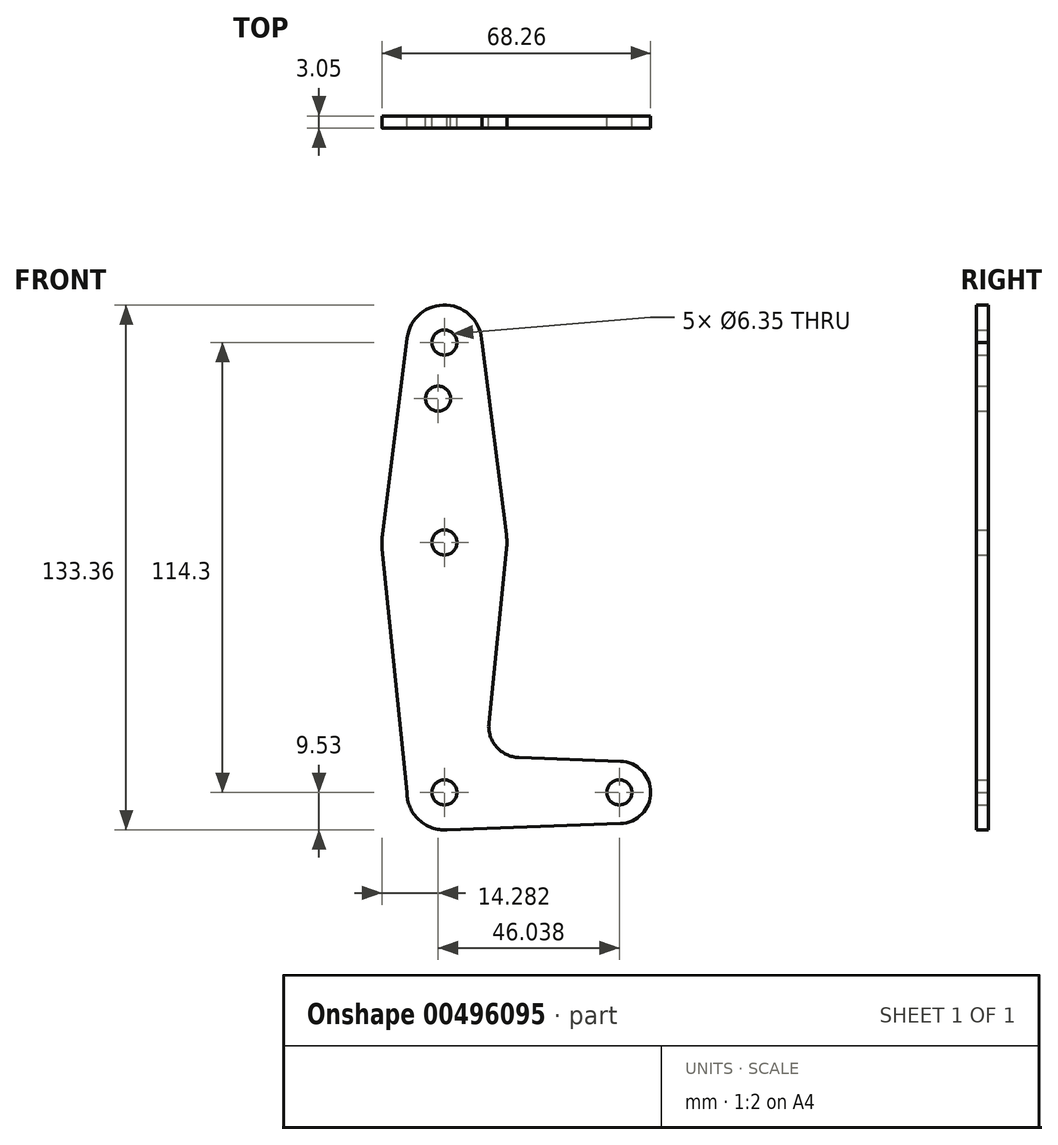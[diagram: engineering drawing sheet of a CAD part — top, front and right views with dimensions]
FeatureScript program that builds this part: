
annotation { "Feature Type Name" : "Feature", "Feature Type Description" : "" }
export const myFeature = defineFeature(function(context is Context, id is Id, definition is map)
    precondition{}
    {
        {
            var Q0;
            Q0=qCreatedBy(makeId("Front.planeOp"),FACE);
            var sketch = newSketch(context, id + "F0", { "sketchPlane" : qUnion([Q0])});
            skLineSegment(sketch, "E0", {"start": v(0, 114.3) * mm, "end": v(0, 0) * mm, "construction": true});
            skLineSegment(sketch, "E1", {"start": v(0, 0) * mm, "end": v(44.45, 0) * mm, "construction": true});
            skCircle(sketch, "E2", {"center": v(0, 0) * mm, "radius": 9.53 * mm});
            skCircle(sketch, "E3", {"center": v(44.45, 0) * mm, "radius": 7.94 * mm});
            skCircle(sketch, "E4", {"center": v(0, 63.5) * mm, "radius": 15.88 * mm});
            skCircle(sketch, "E5", {"center": v(0, 114.3) * mm, "radius": 9.53 * mm});
            skLineSegment(sketch, "E6", {"start": v(9.52, 114.3) * mm, "end": v(15.75, 65.5) * mm});
            skLineSegment(sketch, "E7", {"start": v(-9.45, 115.5) * mm, "end": v(-15.75, 65.48) * mm});
            skLineSegment(sketch, "E8", {"start": v(15.8, 61.9) * mm, "end": v(11.3, 17.6) * mm});
            skLineSegment(sketch, "E9", {"start": v(-15.8, 61.9) * mm, "end": v(-9.52, 0) * mm});
            skLineSegment(sketch, "E10", {"start": v(44.73, 7.93) * mm, "end": v(18.93, 8.85) * mm});
            skCircle(sketch, "E11", {"center": v(0, 114.3) * mm, "radius": 3.18 * mm});
            skCircle(sketch, "E12", {"center": v(0, 63.5) * mm, "radius": 3.18 * mm});
            skCircle(sketch, "E13", {"center": v(0, 0) * mm, "radius": 3.18 * mm});
            skCircle(sketch, "E14", {"center": v(44.45, 0) * mm, "radius": 3.18 * mm});
            skCircle(sketch, "E15", {"center": v(-1.59, 100.03) * mm, "radius": 3.18 * mm});
            skLineSegment(sketch, "E16", {"start": v(0, -9.52) * mm, "end": v(44.73, -7.93) * mm});
            skPoint(sketch, "E17.newPointA", {"position": v(0, 9.53) * mm});
            skArc(sketch, "E17.filletArc", {"start": v(11.3, 17.6) * mm, "mid": v(13.22, 11.57) * mm, "end": v(18.93, 8.85) * mm});
            skSolve(sketch);
        }
        {
            var Q0;
            Q0 = qSketchRegion(id + "F0", true);
            extrude(context, id + "F1", {"entities" : qUnion([Q0]), "depth" : 3.05 * mm});
        }
    });
